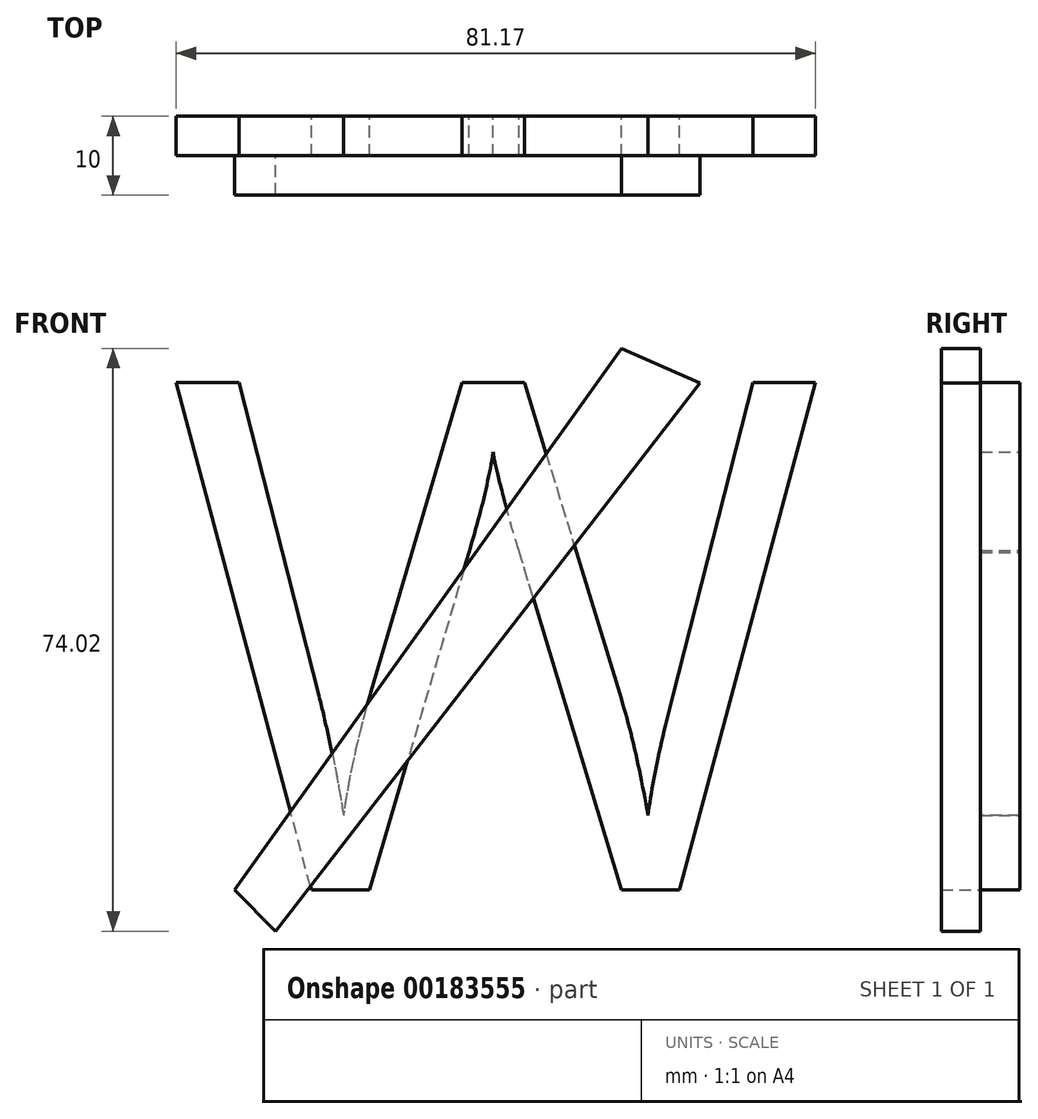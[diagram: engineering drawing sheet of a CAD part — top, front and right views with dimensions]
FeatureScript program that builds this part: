
annotation { "Feature Type Name" : "Feature", "Feature Type Description" : "" }
export const myFeature = defineFeature(function(context is Context, id is Id, definition is map)
    precondition{}
    {
        {
            var Q0;
            Q0=qCreatedBy(makeId("Front.planeOp"),FACE);
            var sketch = newSketch(context, id + "F0", { "sketchPlane" : qUnion([Q0])});
            skText(sketch, "E0", { "text": "W", "fontName": "OpenSans-Regular.ttf"});
            const initialGuessF0  = {"E0": [-0.02476, -0.03575, 1, 0, 0.065]};
            skSetInitialGuess(sketch, initialGuessF0);
            skSolve(sketch);
        }
        {
            var Q0;
            Q0 = qSketchRegion(id + "F0", true);
            extrude(context, id + "F1", {"entities" : qUnion([Q0]), "depth" : 5 * mm});
        }
        {
            var Q0;
            Q0=makeQuery(id+"F1.opExtrude","CAP_FACE",FACE,{"disambiguationData":[OSD([sQuery(id+"F0.wireOp",EDGE,"E0.sketch_text.stroke-0"),sQuery(id+"F0.wireOp",EDGE,"E0.sketch_text.stroke-1"),sQuery(id+"F0.wireOp",EDGE,"E0.sketch_text.stroke-2"),sQuery(id+"F0.wireOp",EDGE,"E0.sketch_text.stroke-3"),sQuery(id+"F0.wireOp",EDGE,"E0.sketch_text.stroke-4"),sQuery(id+"F0.wireOp",EDGE,"E0.sketch_text.stroke-5"),sQuery(id+"F0.wireOp",EDGE,"E0.sketch_text.stroke-6"),sQuery(id+"F0.wireOp",EDGE,"E0.sketch_text.stroke-7"),sQuery(id+"F0.wireOp",EDGE,"E0.sketch_text.stroke-8"),sQuery(id+"F0.wireOp",EDGE,"E0.sketch_text.stroke-9"),sQuery(id+"F0.wireOp",EDGE,"E0.sketch_text.stroke-10"),sQuery(id+"F0.wireOp",EDGE,"E0.sketch_text.stroke-11"),sQuery(id+"F0.wireOp",EDGE,"E0.sketch_text.stroke-12"),sQuery(id+"F0.wireOp",EDGE,"E0.sketch_text.stroke-13"),sQuery(id+"F0.wireOp",EDGE,"E0.sketch_text.stroke-14"),sQuery(id+"F0.wireOp",EDGE,"E0.sketch_text.stroke-15"),sQuery(id+"F0.wireOp",EDGE,"E0.sketch_text.stroke-16"),sQuery(id+"F0.wireOp",EDGE,"E0.sketch_text.stroke-17"),sQuery(id+"F0.wireOp",EDGE,"E0.sketch_text.stroke-18"),sQuery(id+"F0.wireOp",EDGE,"E0.sketch_text.stroke-19")])],"isStart":false});
            var sketch = newSketch(context, id + "F2", { "sketchPlane" : qUnion([Q0])});
            skLineSegment(sketch, "E1", {"start": v(-16.15, -35.75) * mm, "end": v(-10.97, -40.97) * mm});
            skLineSegment(sketch, "E2", {"start": v(-10.97, -40.97) * mm, "end": v(42.95, 28.7) * mm});
            skLineSegment(sketch, "E3", {"start": v(42.95, 28.7) * mm, "end": v(32.95, 33.05) * mm});
            skLineSegment(sketch, "E4", {"start": v(32.95, 33.05) * mm, "end": v(-16.15, -35.75) * mm});
            skSolve(sketch);
        }
        {
            var Q0;
            Q0 = qSketchRegion(id + "F2", true);
            extrude(context, id + "F3", {"entities" : qUnion([Q0]), "operationType" : NewBodyOperationType.ADD, "depth" : 5 * mm});
        }
    });
